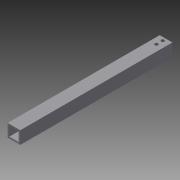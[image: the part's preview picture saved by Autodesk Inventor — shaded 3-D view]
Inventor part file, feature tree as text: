
AUTODESK INVENTOR PART (.ipt)
format: ipt  version: 2013 (Build 170138000, 138)  size: 96,256 bytes
history: native  units: in
note: dims shown in document units (in); Inventor stores cm internally (conversion verified against a paired STEP export)
features: extrude x2, sketch x2, reference x2
ambient origin geometry x8: Origin, YZ Plane, XZ Plane, XY Plane, X Axis, Y Axis, Z Axis, Center Point
bodies: Solid1 (feature_tree)
feature tree (6):
  extrude  "Extrusion1"  Depth=1.0in
  extrude  "Extrusion2"  Depth=12.0in TaperAngle=0.0deg
  sketch  "Sketch1"  dims[d0=1.0in d2=1.0in]
  sketch  "Sketch2"  dims[d3=0.125in d4=12.0in d5=0.0in d6=1.0in d7=0.0in]
  reference  "Reference1"
  reference  "Reference2"
